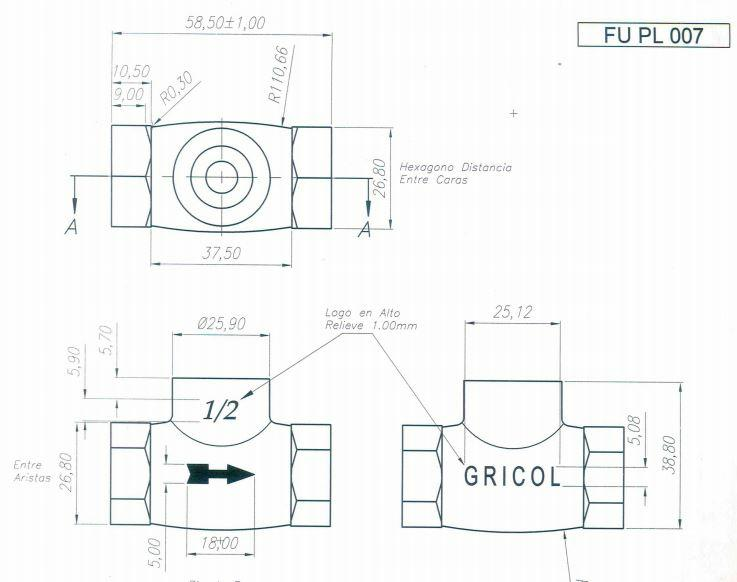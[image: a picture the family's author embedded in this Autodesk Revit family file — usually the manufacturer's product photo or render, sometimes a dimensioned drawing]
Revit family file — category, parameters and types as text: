
# Revit family: 01-1434-11 CONJUNTO REGISTRO DUCHA TOSCANA
name_source: partatom
category: Plumbing Fixtures
revit_build: Autodesk Revit 2018 (Build: 20170223_1515(x64)
units: mm (PartAtom-declared; Revit-internal decimal feet)

## family parameters
Cut with Voids When Loaded = No
Host = Face
OmniClass Number = 23.31.11.00
Part Type = Normal
Room Calculation Point = No
Round Connector Dimension = Use Diameter
Shared = No

## types (1)
- 01-1434-11
    Ancho escudo = 60 mm  [stored 0.19685 ft]
    CW Connection = Yes
    Default Elevation = 0 mm  [stored 0 ft]
    Description = Mezclador ducha
    HW Connection = Yes
    Laton = Laton
    Link Ficha Tecnica = No encontrada en internet
    Manija = 70 mm  [stored 0.229659 ft]
    Manufacturer = Gricol
    Model = 01-1434-11
    Plastico - ABS Cromado = Plastico - ABS Cromado
    Product Name = CONJUNTO REGISTRO DUCHA TOSCANA
    Type Image = LOGO-01.jpg
    URL = https://www.gricol.com
    Vent Connection = No
    Waste Connection = No

note: [stored X ft] marks values corroborated as IEEE doubles in the binary element streams (Revit-internal decimal feet)

## geometry (parser evidence)
native form markers: Blend x4, Sweep x23
no freeform markers — native parametric forms only
